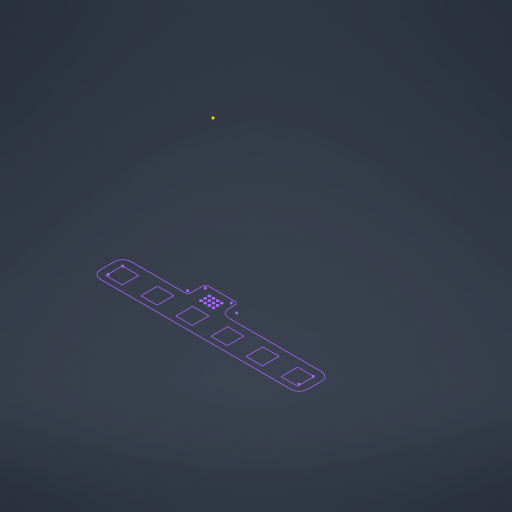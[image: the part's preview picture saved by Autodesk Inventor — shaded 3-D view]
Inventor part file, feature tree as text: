
AUTODESK INVENTOR PART (.ipt)
format: ipt  version: 2024.3 (Build 283343010, 343A)  size: 227,840 bytes
history: native  units: mm
features: sketch x1
ambient origin geometry x8: Origin, YZ Plane, XZ Plane, XY Plane, X Axis, Y Axis, Z Axis, Center Point
feature tree (1):
  sketch  "Skizze1"
